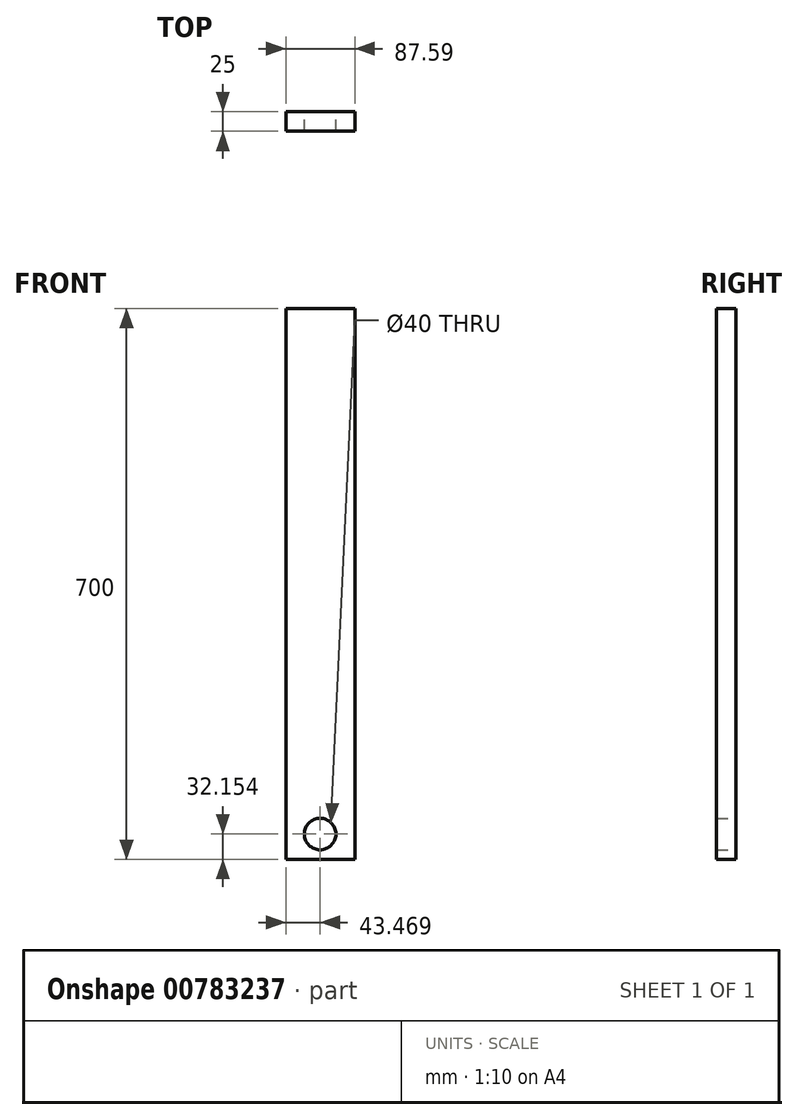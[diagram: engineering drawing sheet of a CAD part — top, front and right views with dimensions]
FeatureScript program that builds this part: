
annotation { "Feature Type Name" : "Feature", "Feature Type Description" : "" }
export const myFeature = defineFeature(function(context is Context, id is Id, definition is map)
    precondition{}
    {
        {
            var Q0;
            Q0=qCreatedBy(makeId("Front.planeOp"),FACE);
            var sketch = newSketch(context, id + "F0", { "sketchPlane" : qUnion([Q0])});
            skLineSegment(sketch, "E0.bottom", {"start": v(64.13, 137.17) * mm, "end": v(-23.46, 137.17) * mm});
            skLineSegment(sketch, "E0.top", {"start": v(64.13, -562.83) * mm, "end": v(-23.46, -562.83) * mm});
            skLineSegment(sketch, "E0.left", {"start": v(64.13, 137.17) * mm, "end": v(64.13, -562.83) * mm});
            skLineSegment(sketch, "E0.right", {"start": v(-23.46, 137.17) * mm, "end": v(-23.46, -562.83) * mm});
            skPoint(sketch, "E0.middle", {"position": v(20.34, -212.83) * mm});
            skCircle(sketch, "E1", {"center": v(20, -530.68) * mm, "radius": 20 * mm});
            skSolve(sketch);
        }
        {
            var Q0;
            Q0=makeQuery(id+"F0.imprint","IMPRINT",FACE,{"disambiguationData":[TD([[makeQuery(id+"F0.imprint","IMPRINT",EDGE,{"derivedFrom":sQuery(id+"F0.wireOp",EDGE,"E0.bottom")}),1.0]])]});
            extrude(context, id + "F1", {"entities" : qUnion([Q0]), "depth" : 25 * mm, "offsetDistance" : 25 * mm});
        }
    });
